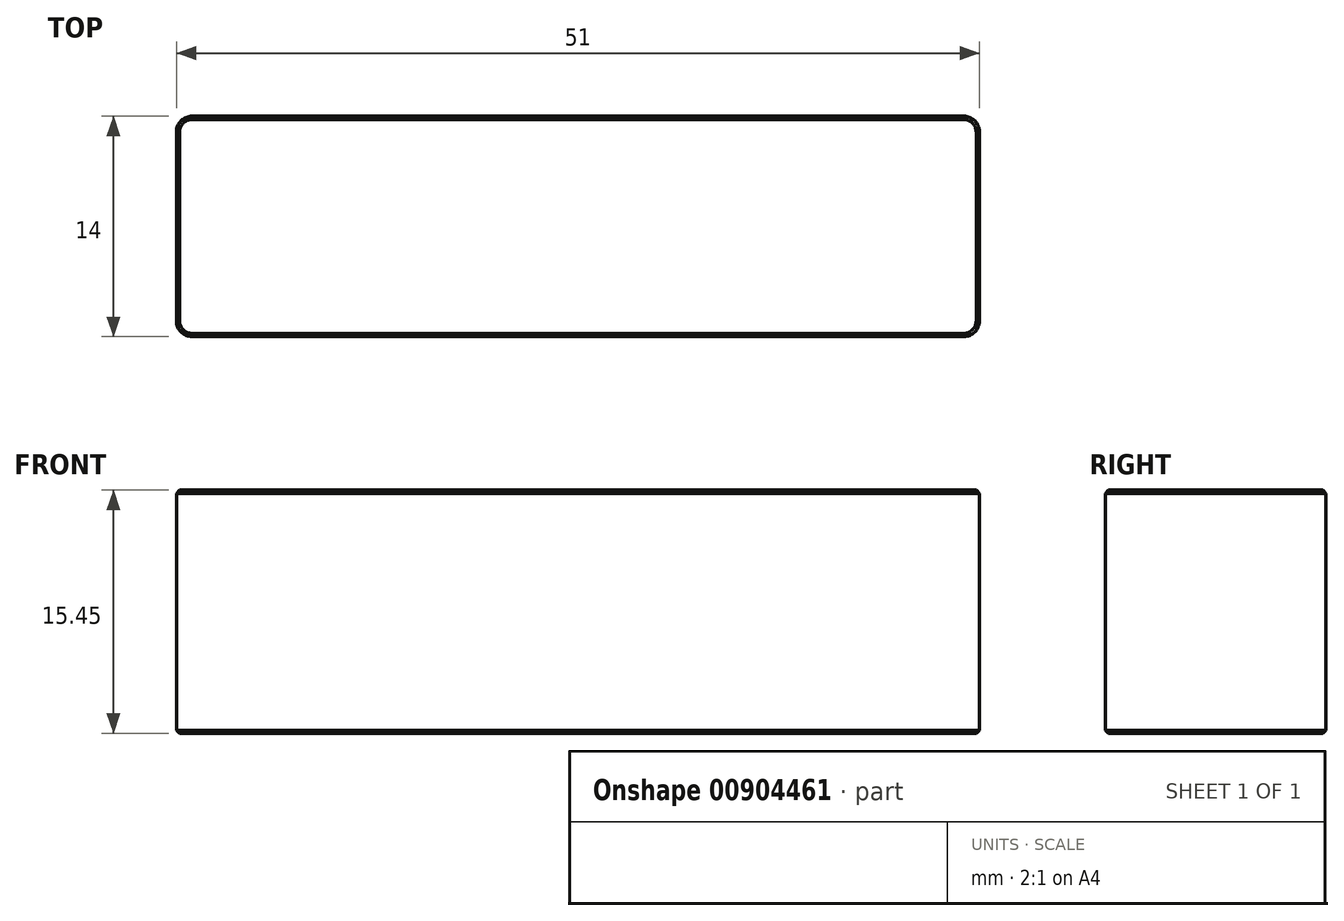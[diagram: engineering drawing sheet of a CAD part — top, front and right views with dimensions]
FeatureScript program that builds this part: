
annotation { "Feature Type Name" : "Feature", "Feature Type Description" : "" }
export const myFeature = defineFeature(function(context is Context, id is Id, definition is map)
    precondition{}
    {
        {
            var Q0;
            Q0=qCreatedBy(makeId("Top.planeOp"),FACE);
            var sketch = newSketch(context, id + "F0", { "sketchPlane" : qUnion([Q0])});
            skLineSegment(sketch, "E0.bottom", {"start": v(-25.5, 7) * mm, "end": v(25.5, 7) * mm});
            skLineSegment(sketch, "E0.top", {"start": v(-25.5, -7) * mm, "end": v(25.5, -7) * mm});
            skLineSegment(sketch, "E0.left", {"start": v(-25.5, 7) * mm, "end": v(-25.5, -7) * mm});
            skLineSegment(sketch, "E0.right", {"start": v(25.5, 7) * mm, "end": v(25.5, -7) * mm});
            skPoint(sketch, "E0.middle", {"position": v(0, 0) * mm});
            skSolve(sketch);
        }
        {
            var Q0;
            Q0=makeQuery(id+"F0.imprint","IMPRINT",FACE,{"disambiguationData":[TD([[makeQuery(id+"F0.imprint","IMPRINT",EDGE,{"derivedFrom":sQuery(id+"F0.wireOp",EDGE,"E0.bottom")}),-1.0]])]});
            extrude(context, id + "F1", {"entities" : qUnion([Q0]), "depth" : 15.45 * mm, "offsetDistance" : 25 * mm});
        }
        {
            var Q0;
            Q0=makeQuery(id+"F1.opExtrude","SWEPT_EDGE",EDGE,{"disambiguationData":[OSD([sQuery(id+"F0.wireOp",EDGE,"E0.top"),sQuery(id+"F0.wireOp",EDGE,"E0.left")])]});
            var Q1;
            Q1=makeQuery(id+"F1.opExtrude","SWEPT_EDGE",EDGE,{"disambiguationData":[OSD([sQuery(id+"F0.wireOp",EDGE,"E0.top"),sQuery(id+"F0.wireOp",EDGE,"E0.right")])]});
            var Q2;
            Q2=makeQuery(id+"F1.opExtrude","SWEPT_EDGE",EDGE,{"disambiguationData":[OSD([sQuery(id+"F0.wireOp",EDGE,"E0.bottom"),sQuery(id+"F0.wireOp",EDGE,"E0.left")])]});
            var Q3;
            Q3=makeQuery(id+"F1.opExtrude","SWEPT_EDGE",EDGE,{"disambiguationData":[OSD([sQuery(id+"F0.wireOp",EDGE,"E0.bottom"),sQuery(id+"F0.wireOp",EDGE,"E0.right")])]});
            fillet(context, id + "F2", {"entities" : qUnion([Q0, Q1, Q2, Q3]), "tangentPropagation" : true, "radius" : 1 * mm, "defaultsChanged" : true, "vertexSettings" : [], "allowEdgeOverflow" : false});
        }
        {
            var Q0;
            Q0=makeQuery(id+"F1.opExtrude","CAP_FACE",FACE,{"disambiguationData":[OSD([sQuery(id+"F0.wireOp",EDGE,"E0.bottom"),sQuery(id+"F0.wireOp",EDGE,"E0.top"),sQuery(id+"F0.wireOp",EDGE,"E0.left"),sQuery(id+"F0.wireOp",EDGE,"E0.right")])],"isStart":false});
            var Q1;
            Q1=makeQuery(id+"F1.opExtrude","CAP_FACE",FACE,{"disambiguationData":[OSD([sQuery(id+"F0.wireOp",EDGE,"E0.bottom"),sQuery(id+"F0.wireOp",EDGE,"E0.top"),sQuery(id+"F0.wireOp",EDGE,"E0.left"),sQuery(id+"F0.wireOp",EDGE,"E0.right")])],"isStart":true});
            chamfer(context, id + "F3", {"entities" : qUnion([Q0, Q1]), "width" : 0.2 * mm, "tangentPropagation" : true});
        }
    });
